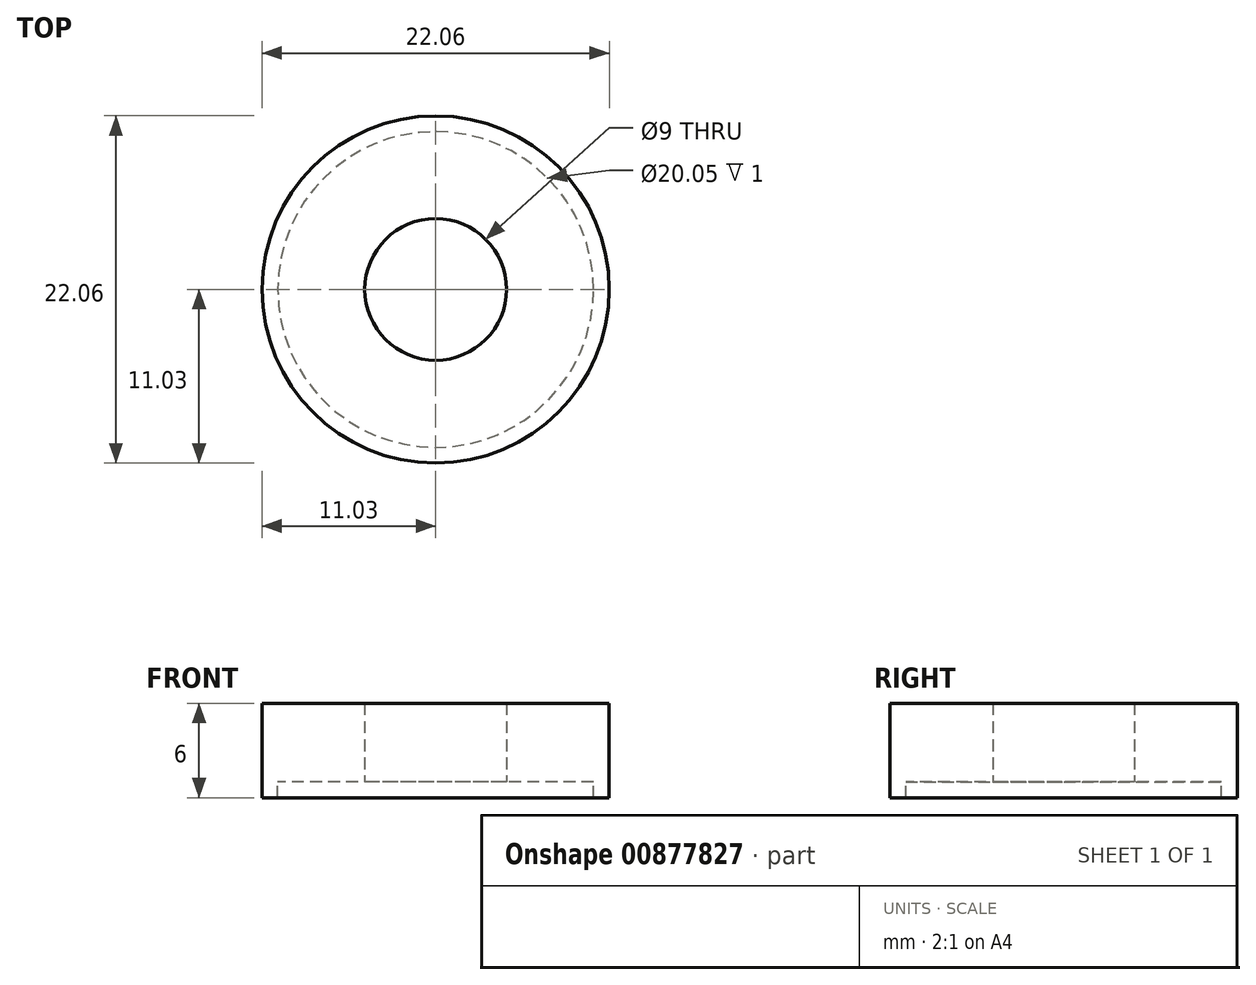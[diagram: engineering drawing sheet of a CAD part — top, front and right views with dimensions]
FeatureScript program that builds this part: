
annotation { "Feature Type Name" : "Feature", "Feature Type Description" : "" }
export const myFeature = defineFeature(function(context is Context, id is Id, definition is map)
    precondition{}
    {
        {
            var Q0;
            Q0=qCreatedBy(makeId("Top.planeOp"),FACE);
            var sketch = newSketch(context, id + "F0", { "sketchPlane" : qUnion([Q0])});
            skCircle(sketch, "E0", {"center": v(0, 0) * mm, "radius": 4.5 * mm});
            skCircle(sketch, "E1", {"center": v(0, 0) * mm, "radius": 3.47 * mm});
            skCircle(sketch, "E2", {"center": v(0, 0) * mm, "radius": 10.02 * mm});
            skCircle(sketch, "E3", {"center": v(0, 0) * mm, "radius": 11.03 * mm});
            skSolve(sketch);
        }
        {
            var Q0;
            Q0=makeQuery(id+"F0.imprint","IMPRINT",FACE,{"disambiguationData":[TD([[makeQuery(id+"F0.imprint","IMPRINT",EDGE,{"derivedFrom":sQuery(id+"F0.wireOp",EDGE,"E0")}),-1.0]])]});
            extrude(context, id + "F1", {"entities" : qUnion([Q0]), "depth" : 1.5 * mm, "offsetDistance" : 25 * mm});
        }
        {
            var Q0;
            Q0 = qSketchRegion(id + "F0", true);
            var Q1;
            Q1=makeQuery(id+"F1.opExtrude","CAP_FACE",FACE,{"disambiguationData":[OSD([sQuery(id+"F0.wireOp",EDGE,"E0"),sQuery(id+"F0.wireOp",EDGE,"E2")])],"isStart":true});
            extrude(context, id + "F2", {"entities" : qUnion([Q0, Q1]), "operationType" : NewBodyOperationType.ADD, "depth" : 2 * mm, "offsetDistance" : 25 * mm});
        }
        {
            var Q0;
            Q0 = qSketchRegion(id + "F0", true);
            extrude(context, id + "F3", {"entities" : qUnion([Q0]), "operationType" : NewBodyOperationType.ADD, "oppositeDirection" : true, "depth" : 2 * mm, "offsetDistance" : 25 * mm});
        }
        {
            var Q0;
            {var subQ0=sQuery(id+"F0.wireOp",EDGE,"E2");var subQ1=sQuery(id+"F0.wireOp",EDGE,"E0");Q0=makeQuery(id+"F2.boolean.opBoolean","MERGE",FACE,{"derivedFrom":[makeQuery(id+"F1.opExtrude","CAP_FACE",FACE,{"disambiguationData":[OSD([subQ1,subQ0])],"isStart":true}),makeQuery(id+"F2.opExtrude","CAP_FACE",FACE,{"disambiguationData":[OSD([subQ0,sQuery(id+"F0.wireOp",EDGE,"E3")])],"isStart":true}),makeQuery(id+"F2.opExtrude","CAP_FACE",FACE,{"disambiguationData":[OSD([subQ1,subQ0])],"isStart":true})]});}
            extrude(context, id + "F4", {"entities" : qUnion([Q0]), "operationType" : NewBodyOperationType.ADD, "depth" : 1.5 * mm, "offsetDistance" : 25 * mm});
        }
        {
            var Q0;
            Q0=makeQuery(id+"F4.opExtrude","CAP_FACE",FACE,{"disambiguationData":[OSD([sQuery(id+"F0.wireOp",EDGE,"E0"),sQuery(id+"F0.wireOp",EDGE,"E2"),sQuery(id+"F0.wireOp",EDGE,"E3")])],"isStart":false});
            extrude(context, id + "F5", {"entities" : qUnion([Q0]), "operationType" : NewBodyOperationType.ADD, "depth" : 1.5 * mm, "offsetDistance" : 25 * mm});
        }
        {
            var Q0;
            Q0=makeQuery(id+"F3.opExtrude","CAP_FACE",FACE,{"disambiguationData":[OSD([sQuery(id+"F0.wireOp",EDGE,"E2"),sQuery(id+"F0.wireOp",EDGE,"E3")])],"isStart":false});
            extrude(context, id + "F6", {"entities" : qUnion([Q0]), "operationType" : NewBodyOperationType.ADD, "depth" : 2 * mm, "offsetDistance" : 25 * mm});
        }
        {
            var Q0;
            Q0=makeQuery(id+"F0.imprint","IMPRINT",FACE,{"disambiguationData":[TD([[makeQuery(id+"F0.imprint","IMPRINT",EDGE,{"derivedFrom":sQuery(id+"F0.wireOp",EDGE,"E0")}),-1.0]])]});
            extrude(context, id + "F7", {"entities" : qUnion([Q0]), "operationType" : NewBodyOperationType.ADD, "oppositeDirection" : true, "depth" : 1.5 * mm, "offsetDistance" : 25 * mm});
        }
    });
